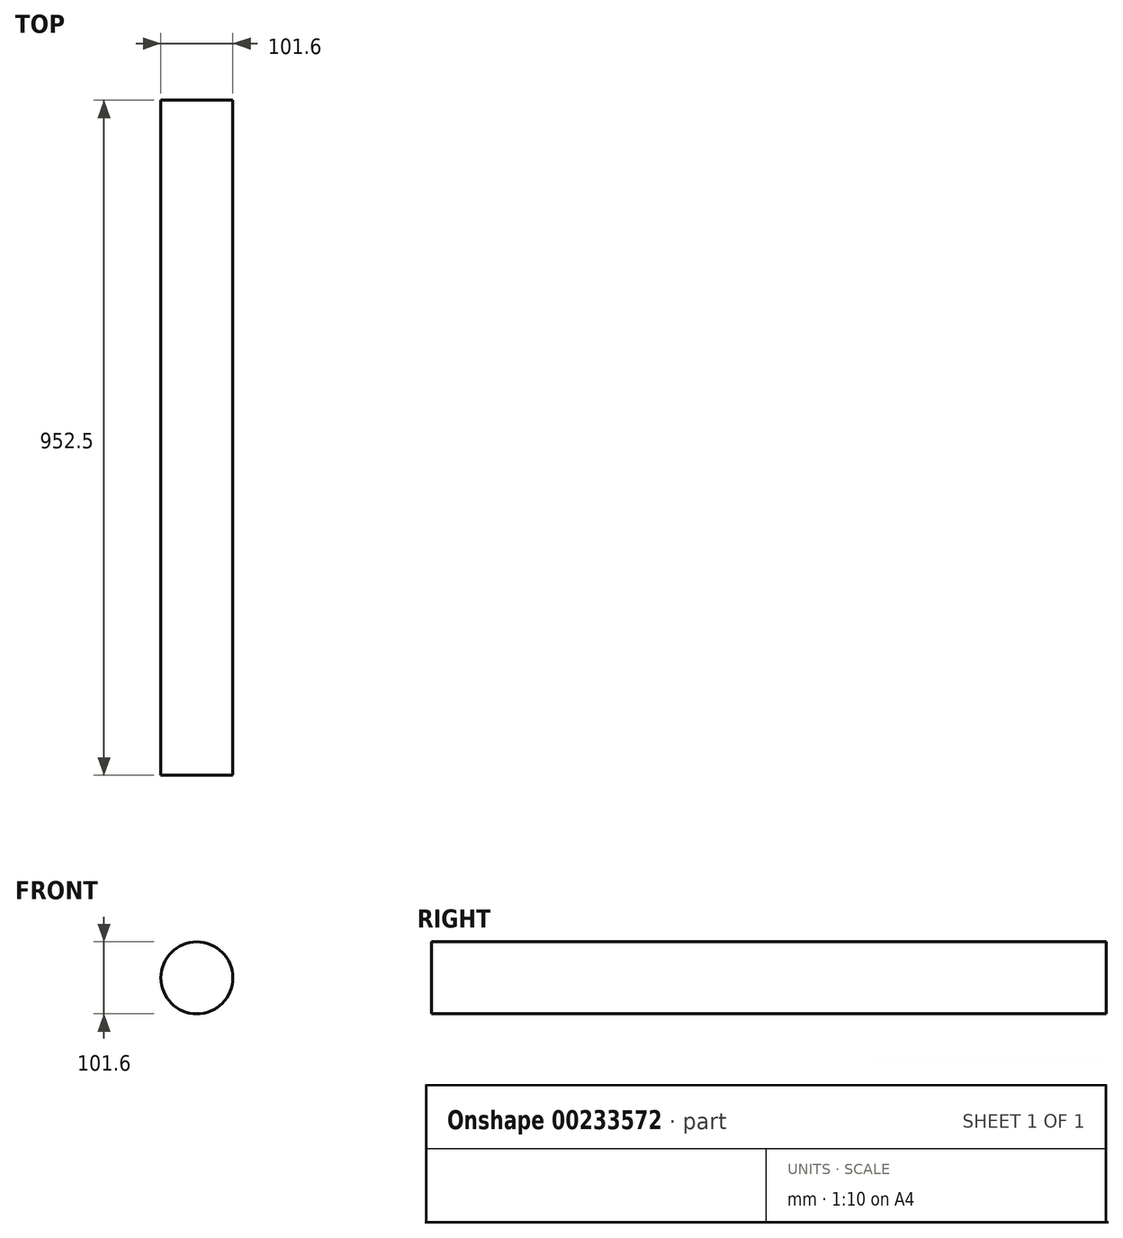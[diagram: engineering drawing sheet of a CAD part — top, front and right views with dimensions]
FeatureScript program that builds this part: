
annotation { "Feature Type Name" : "Feature", "Feature Type Description" : "" }
export const myFeature = defineFeature(function(context is Context, id is Id, definition is map)
    precondition{}
    {
        {
            var Q0;
            Q0=qCreatedBy(makeId("Front.planeOp"),FACE);
            var sketch = newSketch(context, id + "F0", { "sketchPlane" : qUnion([Q0])});
            skCircle(sketch, "E0", {"center": v(0, 0) * mm, "radius": 50.8 * mm});
            skSolve(sketch);
        }
        {
            var Q0;
            Q0=makeQuery(id+"F0.imprint","IMPRINT",FACE,{"disambiguationData":[TD([[makeQuery(id+"F0.imprint","IMPRINT",EDGE,{"derivedFrom":sQuery(id+"F0.wireOp",EDGE,"E0")}),1.0]])]});
            extrude(context, id + "F1", {"entities" : qUnion([Q0]), "depth" : 952.5 * mm});
        }
    });
